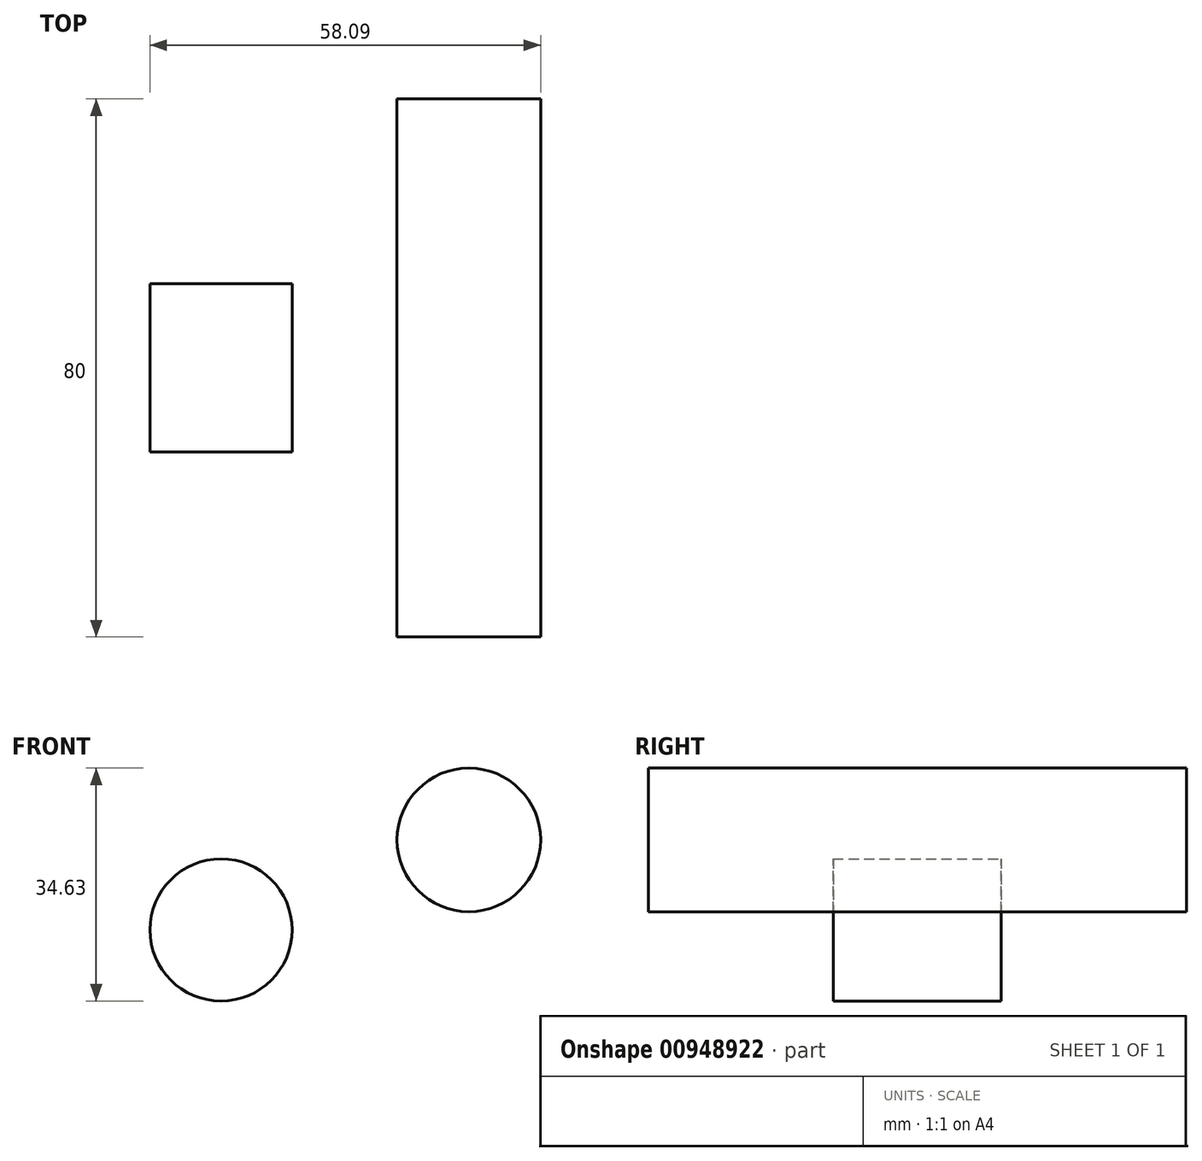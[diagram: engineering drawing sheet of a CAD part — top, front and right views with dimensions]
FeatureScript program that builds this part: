
annotation { "Feature Type Name" : "Feature", "Feature Type Description" : "" }
export const myFeature = defineFeature(function(context is Context, id is Id, definition is map)
    precondition{}
    {
        {
            var Q0;
            Q0=qCreatedBy(makeId("Front.planeOp"),FACE);
            var sketch = newSketch(context, id + "F0", { "sketchPlane" : qUnion([Q0])});
            skCircle(sketch, "E0", {"center": v(0, 0) * mm, "radius": 10.68 * mm});
            skSolve(sketch);
        }
        {
            var Q0;
            Q0=makeQuery(id+"F0.imprint","IMPRINT",FACE,{"disambiguationData":[TD([[makeQuery(id+"F0.imprint","IMPRINT",EDGE,{"derivedFrom":sQuery(id+"F0.wireOp",EDGE,"E0")}),1.0]])]});
            var Q1;
            Q1=sQuery(id+"F0.wireOp",EDGE,"E0");
            extrude(context, id + "F1", {"entities" : qUnion([Q0]), "surfaceEntities" : qUnion([Q1]), "endBound" : BoundingType.SYMMETRIC, "depth" : 80 * mm, "offsetDistance" : 25.4 * mm});
        }
        {
            var Q0;
            Q0=qCreatedBy(makeId("Front.planeOp"),FACE);
            var sketch = newSketch(context, id + "F2", { "sketchPlane" : qUnion([Q0])});
            skCircle(sketch, "E1", {"center": v(-36.85, -13.39) * mm, "radius": 10.57 * mm});
            skSolve(sketch);
        }
        {
            var Q0;
            Q0=makeQuery(id+"F2.imprint","IMPRINT",FACE,{"disambiguationData":[TD([[makeQuery(id+"F2.imprint","IMPRINT",EDGE,{"derivedFrom":sQuery(id+"F2.wireOp",EDGE,"E1")}),1.0]])]});
            var Q1;
            Q1=sQuery(id+"F2.wireOp",EDGE,"E1");
            extrude(context, id + "F3", {"entities" : qUnion([Q0]), "surfaceEntities" : qUnion([Q1]), "endBound" : BoundingType.SYMMETRIC, "depth" : 25 * mm, "offsetDistance" : 25.4 * mm});
        }
    });
